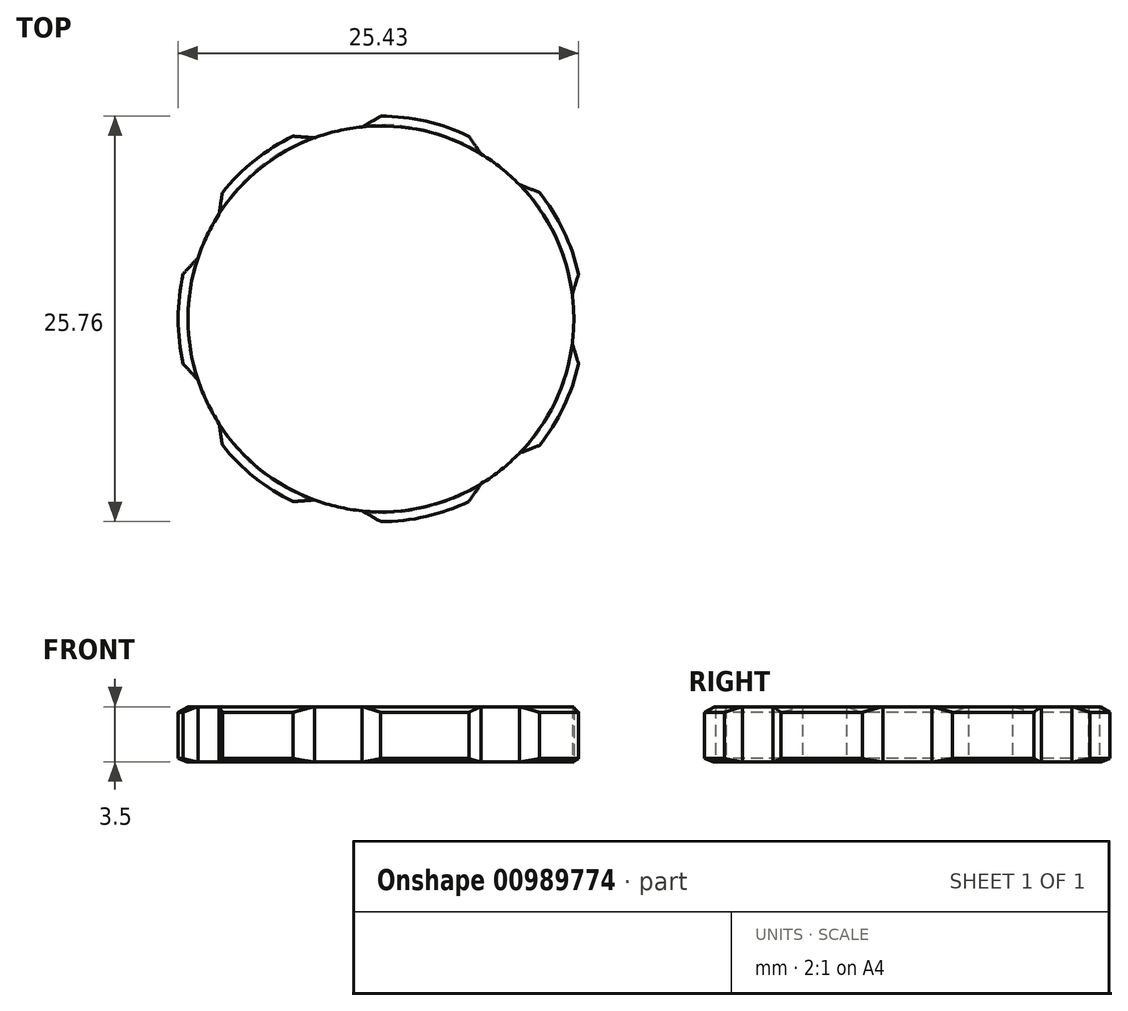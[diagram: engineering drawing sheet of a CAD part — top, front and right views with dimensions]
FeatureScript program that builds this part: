
annotation { "Feature Type Name" : "Feature", "Feature Type Description" : "" }
export const myFeature = defineFeature(function(context is Context, id is Id, definition is map)
    precondition{}
    {
        {
            var Q0;
            Q0=qCreatedBy(makeId("Top.planeOp"),FACE);
            var sketch = newSketch(context, id + "F0", { "sketchPlane" : qUnion([Q0])});
            skCircle(sketch, "E0", {"center": v(0, 0) * mm, "radius": 12.88 * mm});
            skCircle(sketch, "E1", {"center": v(0, 0) * mm, "radius": 12.25 * mm});
            skLineSegment(sketch, "E2", {"start": v(0, 0) * mm, "end": v(-19.77, 0) * mm, "construction": true});
            skLineSegment(sketch, "E3", {"start": v(-12.55, 0) * mm, "end": v(-12.55, -2.88) * mm, "construction": true});
            skLineSegment(sketch, "E4", {"start": v(-12.55, -2.88) * mm, "end": v(0, 0) * mm, "construction": true});
            skLineSegment(sketch, "E5", {"start": v(-12.55, -2.88) * mm, "end": v(-11.62, -3.87) * mm});
            skLineSegment(sketch, "E6.MirrorCS", {"start": v(-12.55, 0) * mm, "end": v(-12.55, 2.88) * mm, "construction": true});
            skLineSegment(sketch, "E7.MirrorCS", {"start": v(-12.55, 2.88) * mm, "end": v(0, 0) * mm, "construction": true});
            skLineSegment(sketch, "E8.MirrorCS", {"start": v(-12.55, 2.88) * mm, "end": v(-11.62, 3.87) * mm});
            skLineSegment(sketch, "E9.1.0", {"start": v(-10.07, -8.02) * mm, "end": v(0, 0) * mm, "construction": true});
            skLineSegment(sketch, "E9.1.1", {"start": v(-5.58, -11.6) * mm, "end": v(0, 0) * mm, "construction": true});
            skLineSegment(sketch, "E9.1.2", {"start": v(-7.82, -9.81) * mm, "end": v(-5.58, -11.6) * mm, "construction": true});
            skLineSegment(sketch, "E9.1.3", {"start": v(-7.82, -9.81) * mm, "end": v(-10.07, -8.02) * mm, "construction": true});
            skLineSegment(sketch, "E9.1.4", {"start": v(-10.07, -8.02) * mm, "end": v(-10.27, -6.67) * mm});
            skLineSegment(sketch, "E9.1.5", {"start": v(-5.58, -11.6) * mm, "end": v(-4.22, -11.5) * mm});
            skLineSegment(sketch, "E9.2.0", {"start": v(-0.01, -12.87) * mm, "end": v(0, 0) * mm, "construction": true});
            skLineSegment(sketch, "E9.2.1", {"start": v(5.6, -11.6) * mm, "end": v(0, 0) * mm, "construction": true});
            skLineSegment(sketch, "E9.2.2", {"start": v(2.8, -12.24) * mm, "end": v(5.6, -11.6) * mm, "construction": true});
            skLineSegment(sketch, "E9.2.3", {"start": v(2.8, -12.24) * mm, "end": v(-0.01, -12.87) * mm, "construction": true});
            skLineSegment(sketch, "E9.2.4", {"start": v(-0.01, -12.87) * mm, "end": v(-1.2, -12.2) * mm});
            skLineSegment(sketch, "E9.2.5", {"start": v(5.6, -11.6) * mm, "end": v(6.36, -10.47) * mm});
            skLineSegment(sketch, "E9.3.0", {"start": v(10.06, -8.04) * mm, "end": v(0, 0) * mm, "construction": true});
            skLineSegment(sketch, "E9.3.1", {"start": v(12.55, -2.85) * mm, "end": v(0, 0) * mm, "construction": true});
            skLineSegment(sketch, "E9.3.2", {"start": v(11.3, -5.45) * mm, "end": v(12.55, -2.85) * mm, "construction": true});
            skLineSegment(sketch, "E9.3.3", {"start": v(11.3, -5.45) * mm, "end": v(10.06, -8.04) * mm, "construction": true});
            skLineSegment(sketch, "E9.3.4", {"start": v(10.06, -8.04) * mm, "end": v(8.79, -8.53) * mm});
            skLineSegment(sketch, "E9.3.5", {"start": v(12.55, -2.85) * mm, "end": v(12.15, -1.55) * mm});
            skLineSegment(sketch, "E9.4.0", {"start": v(12.55, 2.85) * mm, "end": v(0, 0) * mm, "construction": true});
            skLineSegment(sketch, "E9.4.1", {"start": v(10.06, 8.04) * mm, "end": v(0, 0) * mm, "construction": true});
            skLineSegment(sketch, "E9.4.2", {"start": v(11.3, 5.45) * mm, "end": v(10.06, 8.04) * mm, "construction": true});
            skLineSegment(sketch, "E9.4.3", {"start": v(11.3, 5.45) * mm, "end": v(12.55, 2.85) * mm, "construction": true});
            skLineSegment(sketch, "E9.4.4", {"start": v(12.55, 2.85) * mm, "end": v(12.15, 1.55) * mm});
            skLineSegment(sketch, "E9.4.5", {"start": v(10.06, 8.04) * mm, "end": v(8.79, 8.53) * mm});
            skLineSegment(sketch, "E9.5.0", {"start": v(5.6, 11.6) * mm, "end": v(0, 0) * mm, "construction": true});
            skLineSegment(sketch, "E9.5.1", {"start": v(-0.01, 12.87) * mm, "end": v(0, 0) * mm, "construction": true});
            skLineSegment(sketch, "E9.5.2", {"start": v(2.8, 12.24) * mm, "end": v(-0.01, 12.87) * mm, "construction": true});
            skLineSegment(sketch, "E9.5.3", {"start": v(2.8, 12.24) * mm, "end": v(5.6, 11.6) * mm, "construction": true});
            skLineSegment(sketch, "E9.5.4", {"start": v(5.6, 11.6) * mm, "end": v(6.36, 10.47) * mm});
            skLineSegment(sketch, "E9.5.5", {"start": v(-0.01, 12.87) * mm, "end": v(-1.2, 12.2) * mm});
            skLineSegment(sketch, "E9.6.0", {"start": v(-5.58, 11.6) * mm, "end": v(0, 0) * mm, "construction": true});
            skLineSegment(sketch, "E9.6.1", {"start": v(-10.07, 8.02) * mm, "end": v(0, 0) * mm, "construction": true});
            skLineSegment(sketch, "E9.6.2", {"start": v(-7.82, 9.81) * mm, "end": v(-10.07, 8.02) * mm, "construction": true});
            skLineSegment(sketch, "E9.6.3", {"start": v(-7.82, 9.81) * mm, "end": v(-5.58, 11.6) * mm, "construction": true});
            skLineSegment(sketch, "E9.6.4", {"start": v(-5.58, 11.6) * mm, "end": v(-4.22, 11.5) * mm});
            skLineSegment(sketch, "E9.6.5", {"start": v(-10.07, 8.02) * mm, "end": v(-10.27, 6.67) * mm});
            skSolve(sketch);
        }
        {
            var Q0;
            {var subQ0=sQuery(id+"F0.wireOp",EDGE,"E1");var subQ8=makeQuery(id+"F0.imprint","INTERSECT",VERTEX,{"derivedFrom":[subQ0,sQuery(id+"F0.wireOp",EDGE,"E9.4.4")]});Q0=makeQuery(id+"F0.imprint","IMPRINT",FACE,{"disambiguationData":[TD([[makeQuery(id+"F0.imprint","IMPRINT",EDGE,{"disambiguationData":[TD([[subQ8,-1.0]])],"derivedFrom":subQ0}),1.0]])]});}
            var Q1;
            {var subQ0=sQuery(id+"F0.wireOp",EDGE,"E9.6.4");Q1=makeQuery(id+"F0.imprint","IMPRINT",FACE,{"disambiguationData":[TD([[makeQuery(id+"F0.imprint","IMPRINT",EDGE,{"derivedFrom":subQ0}),-1.0]])]});}
            var Q2;
            {var subQ0=sQuery(id+"F0.wireOp",EDGE,"E9.5.4");Q2=makeQuery(id+"F0.imprint","IMPRINT",FACE,{"disambiguationData":[TD([[makeQuery(id+"F0.imprint","IMPRINT",EDGE,{"derivedFrom":subQ0}),-1.0]])]});}
            var Q3;
            {var subQ0=sQuery(id+"F0.wireOp",EDGE,"E9.4.4");Q3=makeQuery(id+"F0.imprint","IMPRINT",FACE,{"disambiguationData":[TD([[makeQuery(id+"F0.imprint","IMPRINT",EDGE,{"derivedFrom":subQ0}),-1.0]])]});}
            var Q4;
            {var subQ0=sQuery(id+"F0.wireOp",EDGE,"E9.3.4");Q4=makeQuery(id+"F0.imprint","IMPRINT",FACE,{"disambiguationData":[TD([[makeQuery(id+"F0.imprint","IMPRINT",EDGE,{"derivedFrom":subQ0}),-1.0]])]});}
            var Q5;
            {var subQ0=sQuery(id+"F0.wireOp",EDGE,"E5");Q5=makeQuery(id+"F0.imprint","IMPRINT",FACE,{"disambiguationData":[TD([[makeQuery(id+"F0.imprint","IMPRINT",EDGE,{"derivedFrom":subQ0}),1.0]])]});}
            var Q6;
            {var subQ0=sQuery(id+"F0.wireOp",EDGE,"E9.1.4");Q6=makeQuery(id+"F0.imprint","IMPRINT",FACE,{"disambiguationData":[TD([[makeQuery(id+"F0.imprint","IMPRINT",EDGE,{"derivedFrom":subQ0}),-1.0]])]});}
            var Q7;
            {var subQ0=sQuery(id+"F0.wireOp",EDGE,"E9.2.4");Q7=makeQuery(id+"F0.imprint","IMPRINT",FACE,{"disambiguationData":[TD([[makeQuery(id+"F0.imprint","IMPRINT",EDGE,{"derivedFrom":subQ0}),-1.0]])]});}
            extrude(context, id + "F1", {"entities" : qUnion([Q0, Q1, Q2, Q3, Q4, Q5, Q6, Q7]), "depth" : 3.5 * mm, "offsetDistance" : 25 * mm});
        }
        {
            var Q0;
            {var subQ0=sQuery(id+"F0.wireOp",EDGE,"E0");Q0=makeQuery(id+"F1.opExtrude","CAP_EDGE",EDGE,{"disambiguationData":[OSD([subQ0]),TDD([makeQuery(id+"F0.imprint","IMPRINT",EDGE,{"disambiguationData":[TD([[makeQuery(id+"F0.imprint","INTERSECT",VERTEX,{"derivedFrom":[subQ0,sQuery(id+"F0.wireOp",EDGE,"E9.1.4")]}),-1.0]])],"derivedFrom":subQ0})])],"isStart":false});}
            var Q1;
            {var subQ0=sQuery(id+"F0.wireOp",EDGE,"E0");Q1=makeQuery(id+"F1.opExtrude","CAP_EDGE",EDGE,{"disambiguationData":[OSD([subQ0]),TDD([makeQuery(id+"F0.imprint","IMPRINT",EDGE,{"disambiguationData":[TD([[makeQuery(id+"F0.imprint","INTERSECT",VERTEX,{"derivedFrom":[subQ0,sQuery(id+"F0.wireOp",EDGE,"E5")]}),1.0]])],"derivedFrom":subQ0})])],"isStart":false});}
            var Q2;
            {var subQ0=sQuery(id+"F0.wireOp",EDGE,"E0");Q2=makeQuery(id+"F1.opExtrude","CAP_EDGE",EDGE,{"disambiguationData":[OSD([subQ0]),TDD([makeQuery(id+"F0.imprint","IMPRINT",EDGE,{"disambiguationData":[TD([[makeQuery(id+"F0.imprint","INTERSECT",VERTEX,{"derivedFrom":[subQ0,sQuery(id+"F0.wireOp",EDGE,"E9.6.4")]}),-1.0]])],"derivedFrom":subQ0})])],"isStart":false});}
            var Q3;
            {var subQ0=sQuery(id+"F0.wireOp",EDGE,"E0");Q3=makeQuery(id+"F1.opExtrude","CAP_EDGE",EDGE,{"disambiguationData":[OSD([subQ0]),TDD([makeQuery(id+"F0.imprint","IMPRINT",EDGE,{"disambiguationData":[TD([[makeQuery(id+"F0.imprint","INTERSECT",VERTEX,{"derivedFrom":[subQ0,sQuery(id+"F0.wireOp",EDGE,"E9.5.4")]}),-1.0]])],"derivedFrom":subQ0})])],"isStart":false});}
            var Q4;
            {var subQ0=sQuery(id+"F0.wireOp",EDGE,"E0");Q4=makeQuery(id+"F1.opExtrude","CAP_EDGE",EDGE,{"disambiguationData":[OSD([subQ0]),TDD([makeQuery(id+"F0.imprint","IMPRINT",EDGE,{"disambiguationData":[TD([[makeQuery(id+"F0.imprint","INTERSECT",VERTEX,{"derivedFrom":[subQ0,sQuery(id+"F0.wireOp",EDGE,"E9.2.4")]}),-1.0]])],"derivedFrom":subQ0})])],"isStart":false});}
            var Q5;
            {var subQ0=sQuery(id+"F0.wireOp",EDGE,"E0");Q5=makeQuery(id+"F1.opExtrude","CAP_EDGE",EDGE,{"disambiguationData":[OSD([subQ0]),TDD([makeQuery(id+"F0.imprint","IMPRINT",EDGE,{"disambiguationData":[TD([[makeQuery(id+"F0.imprint","INTERSECT",VERTEX,{"derivedFrom":[subQ0,sQuery(id+"F0.wireOp",EDGE,"E9.3.4")]}),-1.0]])],"derivedFrom":subQ0})])],"isStart":false});}
            var Q6;
            {var subQ0=sQuery(id+"F0.wireOp",EDGE,"E0");Q6=makeQuery(id+"F1.opExtrude","CAP_EDGE",EDGE,{"disambiguationData":[OSD([subQ0]),TDD([makeQuery(id+"F0.imprint","IMPRINT",EDGE,{"disambiguationData":[TD([[makeQuery(id+"F0.imprint","INTERSECT",VERTEX,{"derivedFrom":[subQ0,sQuery(id+"F0.wireOp",EDGE,"E9.4.4")]}),-1.0]])],"derivedFrom":subQ0})])],"isStart":false});}
            chamfer(context, id + "F2", {"entities" : qUnion([Q0, Q1, Q2, Q3, Q4, Q5, Q6]), "chamferType" : ChamferType.OFFSET_ANGLE, "width" : .62 * mm, "oppositeDirection" : false, "angle" : 30 * degree, "tangentPropagation" : true});
        }
        {
            var Q0;
            {var subQ0=sQuery(id+"F0.wireOp",EDGE,"E0");Q0=makeQuery(id+"F1.opExtrude","CAP_EDGE",EDGE,{"disambiguationData":[OSD([subQ0]),TDD([makeQuery(id+"F0.imprint","IMPRINT",EDGE,{"disambiguationData":[TD([[makeQuery(id+"F0.imprint","INTERSECT",VERTEX,{"derivedFrom":[subQ0,sQuery(id+"F0.wireOp",EDGE,"E9.1.4")]}),-1.0]])],"derivedFrom":subQ0})])],"isStart":true});}
            var Q1;
            {var subQ0=sQuery(id+"F0.wireOp",EDGE,"E0");Q1=makeQuery(id+"F1.opExtrude","CAP_EDGE",EDGE,{"disambiguationData":[OSD([subQ0]),TDD([makeQuery(id+"F0.imprint","IMPRINT",EDGE,{"disambiguationData":[TD([[makeQuery(id+"F0.imprint","INTERSECT",VERTEX,{"derivedFrom":[subQ0,sQuery(id+"F0.wireOp",EDGE,"E9.2.4")]}),-1.0]])],"derivedFrom":subQ0})])],"isStart":true});}
            var Q2;
            {var subQ0=sQuery(id+"F0.wireOp",EDGE,"E0");Q2=makeQuery(id+"F1.opExtrude","CAP_EDGE",EDGE,{"disambiguationData":[OSD([subQ0]),TDD([makeQuery(id+"F0.imprint","IMPRINT",EDGE,{"disambiguationData":[TD([[makeQuery(id+"F0.imprint","INTERSECT",VERTEX,{"derivedFrom":[subQ0,sQuery(id+"F0.wireOp",EDGE,"E9.3.4")]}),-1.0]])],"derivedFrom":subQ0})])],"isStart":true});}
            var Q3;
            {var subQ0=sQuery(id+"F0.wireOp",EDGE,"E0");Q3=makeQuery(id+"F1.opExtrude","CAP_EDGE",EDGE,{"disambiguationData":[OSD([subQ0]),TDD([makeQuery(id+"F0.imprint","IMPRINT",EDGE,{"disambiguationData":[TD([[makeQuery(id+"F0.imprint","INTERSECT",VERTEX,{"derivedFrom":[subQ0,sQuery(id+"F0.wireOp",EDGE,"E9.4.4")]}),-1.0]])],"derivedFrom":subQ0})])],"isStart":true});}
            var Q4;
            {var subQ0=sQuery(id+"F0.wireOp",EDGE,"E0");Q4=makeQuery(id+"F1.opExtrude","CAP_EDGE",EDGE,{"disambiguationData":[OSD([subQ0]),TDD([makeQuery(id+"F0.imprint","IMPRINT",EDGE,{"disambiguationData":[TD([[makeQuery(id+"F0.imprint","INTERSECT",VERTEX,{"derivedFrom":[subQ0,sQuery(id+"F0.wireOp",EDGE,"E5")]}),1.0]])],"derivedFrom":subQ0})])],"isStart":true});}
            var Q5;
            {var subQ0=sQuery(id+"F0.wireOp",EDGE,"E0");Q5=makeQuery(id+"F1.opExtrude","CAP_EDGE",EDGE,{"disambiguationData":[OSD([subQ0]),TDD([makeQuery(id+"F0.imprint","IMPRINT",EDGE,{"disambiguationData":[TD([[makeQuery(id+"F0.imprint","INTERSECT",VERTEX,{"derivedFrom":[subQ0,sQuery(id+"F0.wireOp",EDGE,"E9.6.4")]}),-1.0]])],"derivedFrom":subQ0})])],"isStart":true});}
            var Q6;
            {var subQ0=sQuery(id+"F0.wireOp",EDGE,"E0");Q6=makeQuery(id+"F1.opExtrude","CAP_EDGE",EDGE,{"disambiguationData":[OSD([subQ0]),TDD([makeQuery(id+"F0.imprint","IMPRINT",EDGE,{"disambiguationData":[TD([[makeQuery(id+"F0.imprint","INTERSECT",VERTEX,{"derivedFrom":[subQ0,sQuery(id+"F0.wireOp",EDGE,"E9.5.4")]}),-1.0]])],"derivedFrom":subQ0})])],"isStart":true});}
            chamfer(context, id + "F3", {"entities" : qUnion([Q0, Q1, Q2, Q3, Q4, Q5, Q6]), "chamferType" : ChamferType.OFFSET_ANGLE, "width" : .2 * mm, "oppositeDirection" : false, "angle" : 70 * degree, "tangentPropagation" : true});
        }
    });
